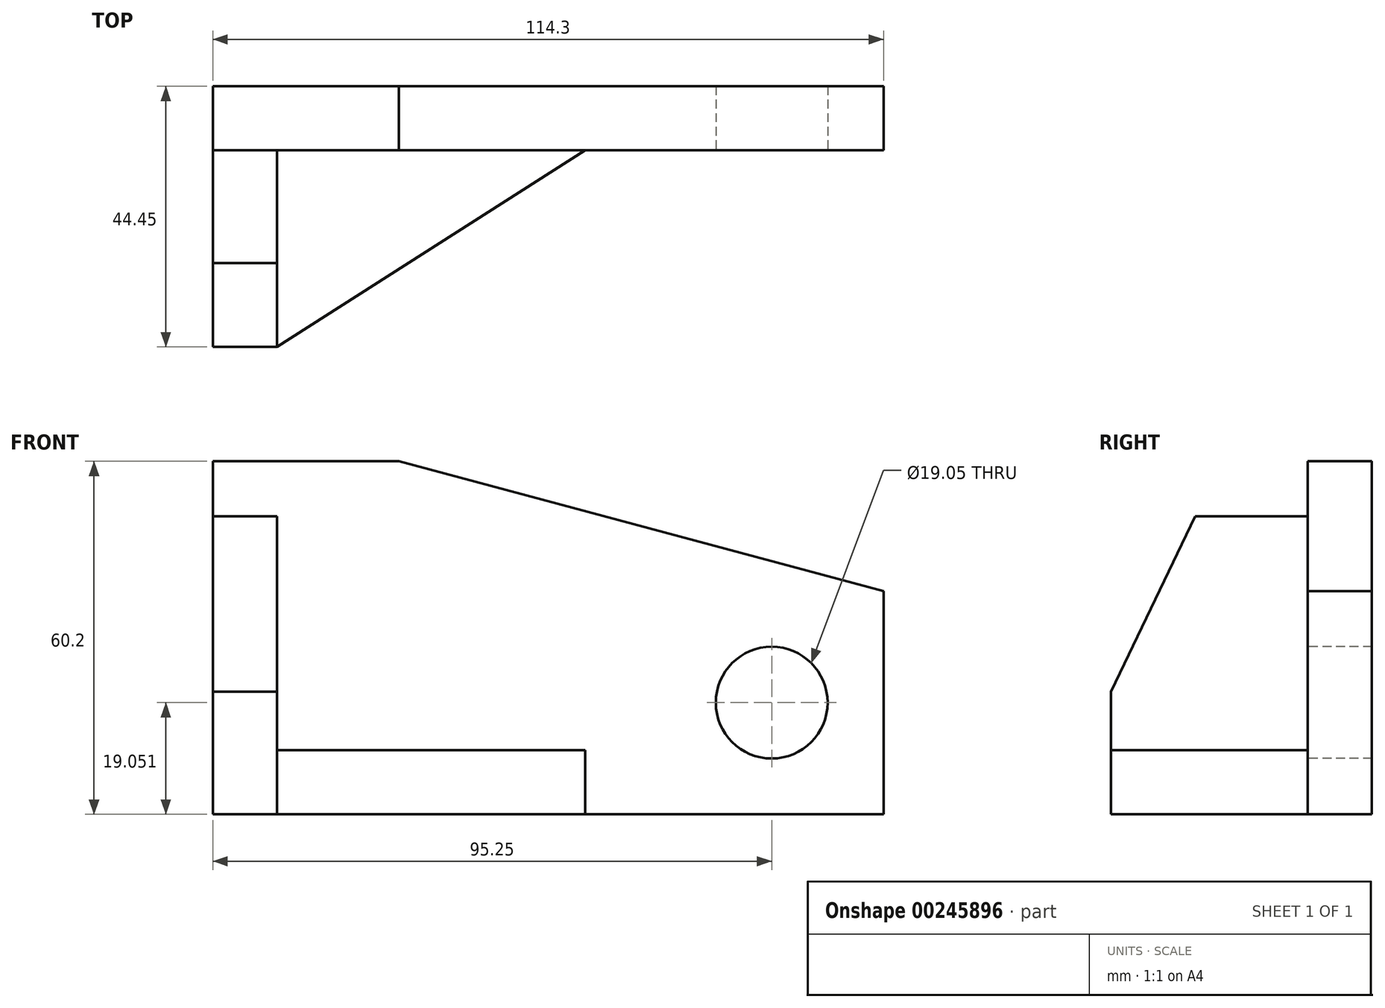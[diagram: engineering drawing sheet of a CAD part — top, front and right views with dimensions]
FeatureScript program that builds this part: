
annotation { "Feature Type Name" : "Feature", "Feature Type Description" : "" }
export const myFeature = defineFeature(function(context is Context, id is Id, definition is map)
    precondition{}
    {
        {
            var Q0;
            Q0=qCreatedBy(makeId("Front.planeOp"),FACE);
            var sketch = newSketch(context, id + "F0", { "sketchPlane" : qUnion([Q0])});
            skLineSegment(sketch, "E0.bottom", {"start": v(57.15, -30.1) * mm, "end": v(-57.15, -30.1) * mm});
            skLineSegment(sketch, "E0.left", {"start": v(57.15, -30.1) * mm, "end": v(57.15, 7.98) * mm});
            skLineSegment(sketch, "E0.right", {"start": v(-57.15, -30.1) * mm, "end": v(-57.15, 30.1) * mm});
            skPoint(sketch, "E0.middle", {"position": v(0, 0) * mm});
            skLineSegment(sketch, "E1", {"start": v(-57.15, 30.1) * mm, "end": v(-25.4, 30.1) * mm});
            skLineSegment(sketch, "E2", {"start": v(-25.4, 30.1) * mm, "end": v(57.15, 7.98) * mm});
            skPoint(sketch, "E3.orphan", {"position": v(57.15, 30.1) * mm});
            skSolve(sketch);
        }
        {
            var Q0;
            Q0=makeQuery(id+"F0.imprint","IMPRINT",FACE,{"disambiguationData":[TD([[makeQuery(id+"F0.imprint","IMPRINT",EDGE,{"derivedFrom":sQuery(id+"F0.wireOp",EDGE,"E0.bottom")}),-1.0]])]});
            extrude(context, id + "F1", {"entities" : qUnion([Q0]), "depth" : 10.92 * mm});
        }
        {
            var Q0;
            Q0=makeQuery(id+"F1.opExtrude","CAP_FACE",FACE,{"disambiguationData":[OSD([sQuery(id+"F0.wireOp",EDGE,"E0.bottom"),sQuery(id+"F0.wireOp",EDGE,"E0.left"),sQuery(id+"F0.wireOp",EDGE,"E0.right"),sQuery(id+"F0.wireOp",EDGE,"E1"),sQuery(id+"F0.wireOp",EDGE,"E2")])],"isStart":false});
            var sketch = newSketch(context, id + "F2", { "sketchPlane" : qUnion([Q0])});
            skLineSegment(sketch, "E4.bottom", {"start": v(-57.15, -30.1) * mm, "end": v(-46.23, -30.1) * mm});
            skLineSegment(sketch, "E4.top", {"start": v(-57.15, 20.7) * mm, "end": v(-46.23, 20.7) * mm});
            skLineSegment(sketch, "E4.left", {"start": v(-57.15, -30.1) * mm, "end": v(-57.15, 20.7) * mm});
            skLineSegment(sketch, "E4.right", {"start": v(-46.23, -30.1) * mm, "end": v(-46.23, 20.7) * mm});
            skSolve(sketch);
        }
        {
            var Q0;
            Q0=makeQuery(id+"F2.imprint","IMPRINT",FACE,{"disambiguationData":[TD([[makeQuery(id+"F2.imprint","IMPRINT",EDGE,{"derivedFrom":sQuery(id+"F2.wireOp",EDGE,"E4.bottom")}),-1.0]])]});
            extrude(context, id + "F3", {"entities" : qUnion([Q0]), "operationType" : NewBodyOperationType.ADD, "depth" : 33.53 * mm});
        }
        {
            var Q0;
            Q0=makeQuery(id+"F3.opExtrude","SWEPT_FACE",FACE,{"disambiguationData":[OSD([sQuery(id+"F2.wireOp",EDGE,"E4.right")])]});
            var sketch = newSketch(context, id + "F4", { "sketchPlane" : qUnion([Q0])});
            skPoint(sketch, "E5", {"position": v(-44.45, -9.18) * mm});
            skLineSegment(sketch, "E6", {"start": v(-44.45, -9.18) * mm, "end": v(-30.11, 20.7) * mm});
            skSolve(sketch);
        }
        {
            var Q0;
            {var subQ0=sQuery(id+"F4.wireOp",EDGE,"E6");Q0=makeQuery(id+"F4.imprint","IMPRINT",FACE,{"disambiguationData":[TD([[makeQuery(id+"F4.imprint","IMPRINT",EDGE,{"derivedFrom":subQ0}),1.0]])]});}
            extrude(context, id + "F5", {"entities" : qUnion([Q0]), "operationType" : NewBodyOperationType.REMOVE, "oppositeDirection" : true, "depth" : 25.4 * mm});
        }
        {
            var Q0;
            Q0=makeQuery(id+"F1.opExtrude","CAP_FACE",FACE,{"disambiguationData":[OSD([sQuery(id+"F0.wireOp",EDGE,"E0.bottom"),sQuery(id+"F0.wireOp",EDGE,"E0.left"),sQuery(id+"F0.wireOp",EDGE,"E0.right"),sQuery(id+"F0.wireOp",EDGE,"E1"),sQuery(id+"F0.wireOp",EDGE,"E2")])],"isStart":false});
            var sketch = newSketch(context, id + "F6", { "sketchPlane" : qUnion([Q0])});
            skLineSegment(sketch, "E7.bottom", {"start": v(-46.23, -30.1) * mm, "end": v(6.35, -30.1) * mm});
            skLineSegment(sketch, "E7.top", {"start": v(-46.23, -19.18) * mm, "end": v(6.35, -19.18) * mm});
            skLineSegment(sketch, "E7.left", {"start": v(-46.23, -30.1) * mm, "end": v(-46.23, -19.18) * mm});
            skLineSegment(sketch, "E7.right", {"start": v(6.35, -30.1) * mm, "end": v(6.35, -19.18) * mm});
            skSolve(sketch);
        }
        {
            var Q0;
            Q0 = qSketchRegion(id + "F6", true);
            extrude(context, id + "F7", {"entities" : qUnion([Q0]), "operationType" : NewBodyOperationType.ADD, "depth" : 33.53 * mm});
        }
        {
            var Q0;
            Q0=makeQuery(id+"F7.opExtrude","SWEPT_FACE",FACE,{"disambiguationData":[OSD([sQuery(id+"F6.wireOp",EDGE,"E7.top")])]});
            var sketch = newSketch(context, id + "F8", { "sketchPlane" : qUnion([Q0])});
            skLineSegment(sketch, "E8", {"start": v(-46.23, -44.45) * mm, "end": v(6.35, -10.92) * mm});
            skSolve(sketch);
        }
        {
            var Q0;
            Q0=makeQuery(id+"F8.imprint","IMPRINT",FACE,{"disambiguationData":[TD([[makeQuery(id+"F8.imprint","IMPRINT",EDGE,{"derivedFrom":sQuery(id+"F8.wireOp",EDGE,"E8")}),-1.0]])]});
            extrude(context, id + "F9", {"entities" : qUnion([Q0]), "operationType" : NewBodyOperationType.REMOVE, "oppositeDirection" : true, "depth" : 10.92 * mm});
        }
        {
            var Q0;
            Q0=makeQuery(id+"F1.opExtrude","CAP_FACE",FACE,{"disambiguationData":[OSD([sQuery(id+"F0.wireOp",EDGE,"E0.bottom"),sQuery(id+"F0.wireOp",EDGE,"E0.left"),sQuery(id+"F0.wireOp",EDGE,"E0.right"),sQuery(id+"F0.wireOp",EDGE,"E1"),sQuery(id+"F0.wireOp",EDGE,"E2")])],"isStart":false});
            var sketch = newSketch(context, id + "F10", { "sketchPlane" : qUnion([Q0])});
            skCircle(sketch, "E9", {"center": v(38.1, -11.05) * mm, "radius": 9.53 * mm});
            skSolve(sketch);
        }
        {
            var Q0;
            Q0=makeQuery(id+"F10.imprint","IMPRINT",FACE,{"disambiguationData":[TD([[makeQuery(id+"F10.imprint","IMPRINT",EDGE,{"derivedFrom":sQuery(id+"F10.wireOp",EDGE,"E9")}),1.0]])]});
            extrude(context, id + "F11", {"entities" : qUnion([Q0]), "operationType" : NewBodyOperationType.REMOVE, "oppositeDirection" : true, "depth" : 15.75 * mm});
        }
    });
